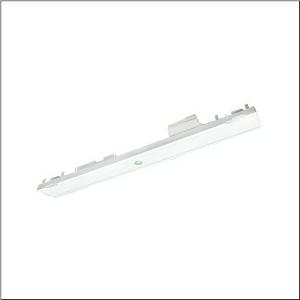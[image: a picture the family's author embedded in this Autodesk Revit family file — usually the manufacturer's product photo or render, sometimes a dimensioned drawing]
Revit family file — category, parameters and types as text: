
# Revit family: licross_56tl157c4x31
name_source: partatom
category: Lighting Fixtures
units: mm (PartAtom-declared; Revit-internal decimal feet)

## family parameters
Cut with Voids When Loaded = No
Host = Face
Light Source = No
Part Type = Normal
Room Calculation Point = No
Round Connector Dimension = Use Diameter
Shared = No

## types (1)
- Licross (1 x LED, 320 lm, 3.9 W, 4000K)
    Apparent Load = 4 VA
    CIE Flux Codes = 31 68 99 100 100
    Color Rendering = 70
    Color Temperature = 4000K
    Default Elevation = 1800 mm
    Description = Licross, luminaire insert, of sheet steel, coil coated, white, length: 500mm, width: 59mm, height: 60mm, mounting height: 2.5..7m, emergency light element,LED rated luminous flux: 320lm, light colour: 740, control gear: CEAG, with plug, 6-pole, with phase selection, mains connection: 220..240V, AC/DC, 0/50..60Hz, rated input power: 3.9W, internal wiring halogen-free, for trunking rail, 9..14-core, for emergency light function, supply monitoring module CEAG, with address switch, choice between two emergency light lines via tool-free moving of contact pin prior to installation in trunking rail, primary light control with lens, of PMMA, primary optical cover: cover, of PMMA, light emission: direct distribution, primary light characteristic: symmetric,  for area, compatible with all CEAG STAR technology systems (ZB-S, DG-S (DualGuard-S), LP-STAR, AT-S+), protection rating (complete): IP40, insulation class (complete): insulation class I (protective earthing), certification: CE, UKCA, protection symbol: D if used in an environment without relevant dust loads, impact resistance: IK06, permissible ambient temperature for indoor applications: -20..+40°C, packaging unit: 1 piece
    Height = 60 mm  [stored 0.19685 ft]
    Lamp = 1 x LED
    Lamp Light Flux = 320 lm
    Lamp Power = 3.9 W
    Lamp count = 1
    Length = 500 mm
    Luminous efficacy = 82 lm/W
    Manufacturer = Siteco
    ModVariant = No
    Model = 56TL157C4X31
    Mounting Place = Ceiling
    Mounting Type = Pendant
    Number of Poles = 1
    OnlyDefault = Yes
    Power Factor = 1
    Product Name = Licross
    Product group = luminaire insert | ceiling pendant
    ProductGroupID = 901
    Protection Class = Protection class I
    Protection Degree = IP 40
    RLX_Detail_Level = 1
    RLX_Emergency_Light_Flux = 0 lm
    RLX_Emergency_Type = 0
    RLX_Emergency_Type_DB = No
    RlxData = <blob elided: 14337 chars, md5=9c77b6ec>
    Socket = socket
    Standby Power = 0 W
    System Light Flux = 320 lm
    System Power = 4 W
    Type Comments = Product without accessories
    Type Image = l_1251804.jpg
    URL = http://relux.com
    VarID = ---
    Voltage = 0 V
    Weight = 0.00 kg
    Width = 59 mm

note: [stored X ft] marks values corroborated as IEEE doubles in the binary element streams (Revit-internal decimal feet)

## geometry (parser evidence)
native form markers: Sweep x9
no freeform markers — native parametric forms only
